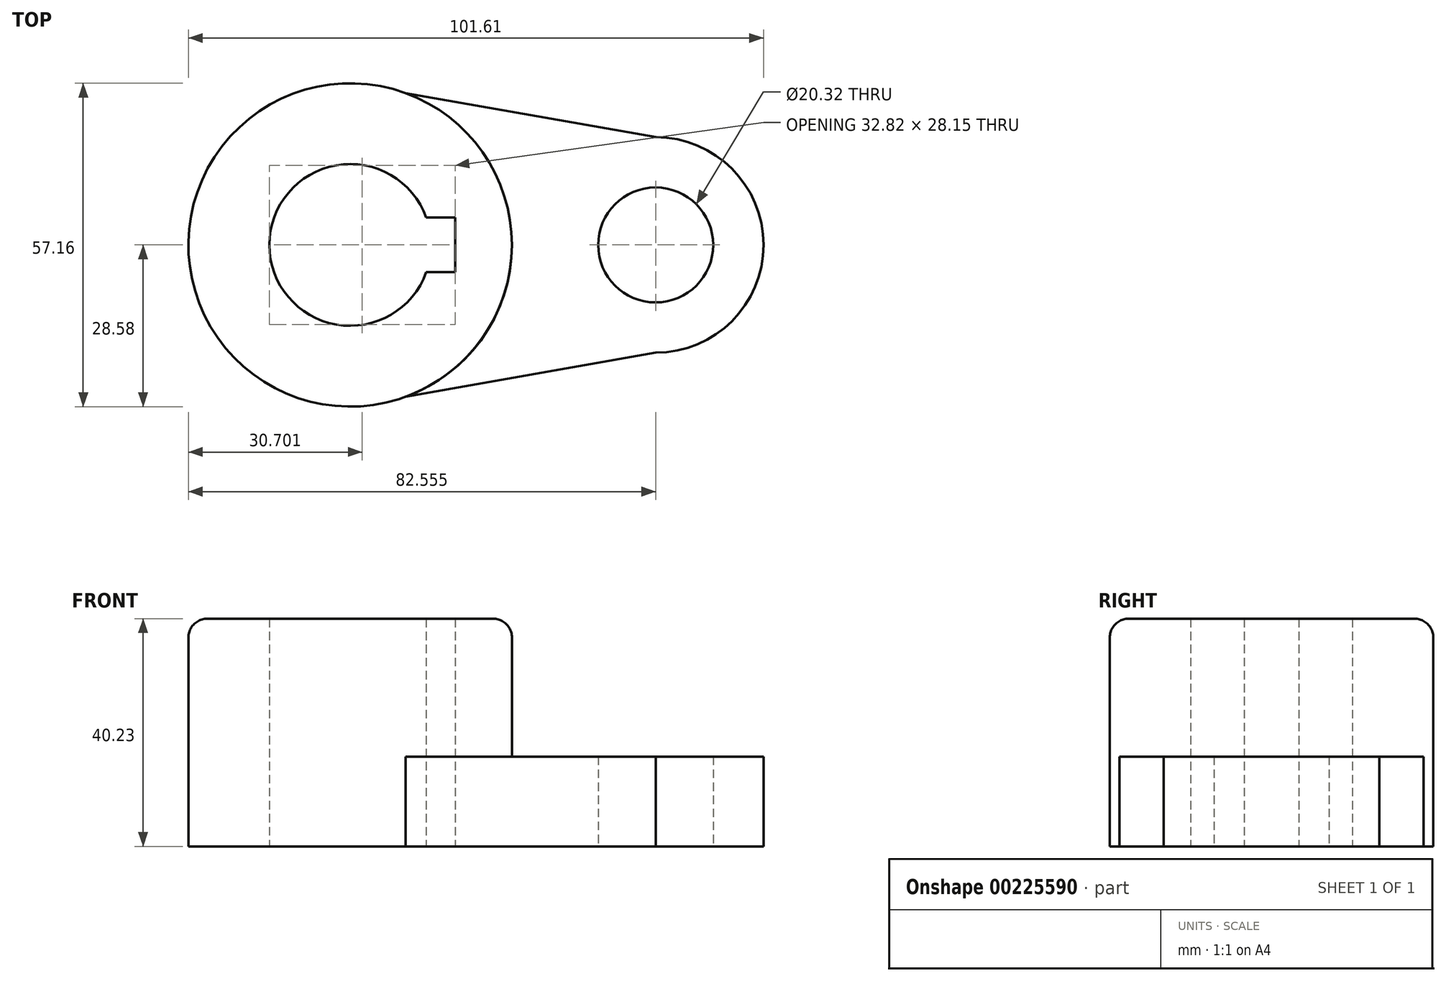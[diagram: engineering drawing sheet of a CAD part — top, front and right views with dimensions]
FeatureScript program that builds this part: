
annotation { "Feature Type Name" : "Feature", "Feature Type Description" : "" }
export const myFeature = defineFeature(function(context is Context, id is Id, definition is map)
    precondition{}
    {
        {
            var Q0;
            Q0=qCreatedBy(makeId("Top.planeOp"),FACE);
            var sketch = newSketch(context, id + "F0", { "sketchPlane" : qUnion([Q0])});
            skCircle(sketch, "E0", {"center": v(0, 0) * mm, "radius": 28.58 * mm});
            skCircle(sketch, "E1", {"center": v(0, 0) * mm, "radius": 14.29 * mm});
            skLineSegment(sketch, "E2.bottom", {"start": v(18.53, -4.83) * mm, "end": v(-13.45, -4.83) * mm});
            skLineSegment(sketch, "E2.top", {"start": v(18.53, 4.83) * mm, "end": v(-13.45, 4.83) * mm});
            skLineSegment(sketch, "E2.left", {"start": v(18.53, -4.83) * mm, "end": v(18.53, 4.83) * mm});
            skPoint(sketch, "E3.endSnap0", {"position": v(0, -4.83) * mm});
            skCircle(sketch, "E4", {"center": v(53.97, 0) * mm, "radius": 10.16 * mm});
            skLineSegment(sketch, "E5", {"start": v(9.78, 26.85) * mm, "end": v(53.98, 19.05) * mm});
            skLineSegment(sketch, "E6", {"start": v(9.78, -26.85) * mm, "end": v(53.97, -19.05) * mm});
            skArc(sketch, "E7", {"start": v(53.97, -19.05) * mm, "mid": v(73.03, 0) * mm, "end": v(53.98, 19.05) * mm});
            skPoint(sketch, "E8.orphan", {"position": v(0, 28.57) * mm});
            skPoint(sketch, "E9.orphan", {"position": v(0, -28.57) * mm});
            skPoint(sketch, "E2.right.start.orphan", {"position": v(-18.53, -4.83) * mm});
            skPoint(sketch, "E10.orphan", {"position": v(-18.53, 4.83) * mm});
            skSolve(sketch);
        }
        {
            var Q0;
            {var subQ5=sQuery(id+"F0.wireOp",EDGE,"E2.left");Q0=makeQuery(id+"F0.imprint","IMPRINT",FACE,{"disambiguationData":[TD([[makeQuery(id+"F0.imprint","IMPRINT",EDGE,{"derivedFrom":subQ5}),-1.0]])]});}
            extrude(context, id + "F1", {"entities" : qUnion([Q0]), "depth" : 40.23 * mm});
        }
        {
            var Q0;
            Q0 = qSketchRegion(id + "F0", true);
            extrude(context, id + "F2", {"entities" : qUnion([Q0]), "operationType" : NewBodyOperationType.ADD, "depth" : 15.88 * mm});
        }
        {
            var Q0;
            Q0=makeQuery(id+"F1.opExtrude","CAP_EDGE",EDGE,{"disambiguationData":[OSD([sQuery(id+"F0.wireOp",EDGE,"E0")])],"isStart":false});
            fillet(context, id + "F3", {"entities" : qUnion([Q0]), "radius" : 3.3 * mm, "tangentPropagation" : true, "allowEdgeOverflow" : false});
        }
    });
